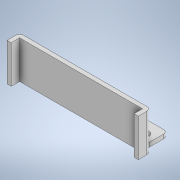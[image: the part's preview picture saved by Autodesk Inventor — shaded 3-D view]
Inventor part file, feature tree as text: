
AUTODESK INVENTOR PART (.ipt)
format: ipt  version: 2020 (Build 240168000, 168)  size: 171,008 bytes
history: native  units: mm
features: extrude x5, sketch x5, other x1, fillet x1
ambient origin geometry x8: Origin, YZ Plane, XZ Plane, XY Plane, X Axis, Y Axis, Z Axis, Center Point
bodies: Body1 (feature_tree)
feature tree (12):
  other  "Sólido1"
  extrude  "Extrusão1"  Depth=18.0mm
  extrude  "Extrusão2"  Depth=2.0mm
  extrude  "Extrusão3"  Depth=4.0mm TaperAngle=0.0deg
  extrude  "Extrusão4"  Depth=10.5mm TaperAngle=0.0deg
  extrude  "Extrusão5"  Depth=2.0mm
  fillet  "Arredondamento3"  Radius=7.425mm
  sketch  "Esboço1"  dims[d0=62.6mm d1=18.0mm]
  sketch  "Esboço2"  dims[d2=2.0mm d3=0.0mm d4=2.0mm]
  sketch  "Esboço3"  dims[d5=2.0mm d6=4.0mm d7=0.0mm]
  sketch  "Esboço4"  dims[d8=2.0mm d9=10.5mm d10=0.0mm]
  sketch  "Esboço5"  dims[d11=4.85mm d12=4.85mm d16=7.425mm d23=47.75mm d25=7.425mm d26=3.925mm d27=3.925mm d28=6.575mm d29=10.5mm d30=0.0mm d32=57.5mm d33=2.55mm d34=2.55mm d35=10.5mm d36=0.0mm d38=2.0mm d39=52.6mm]
